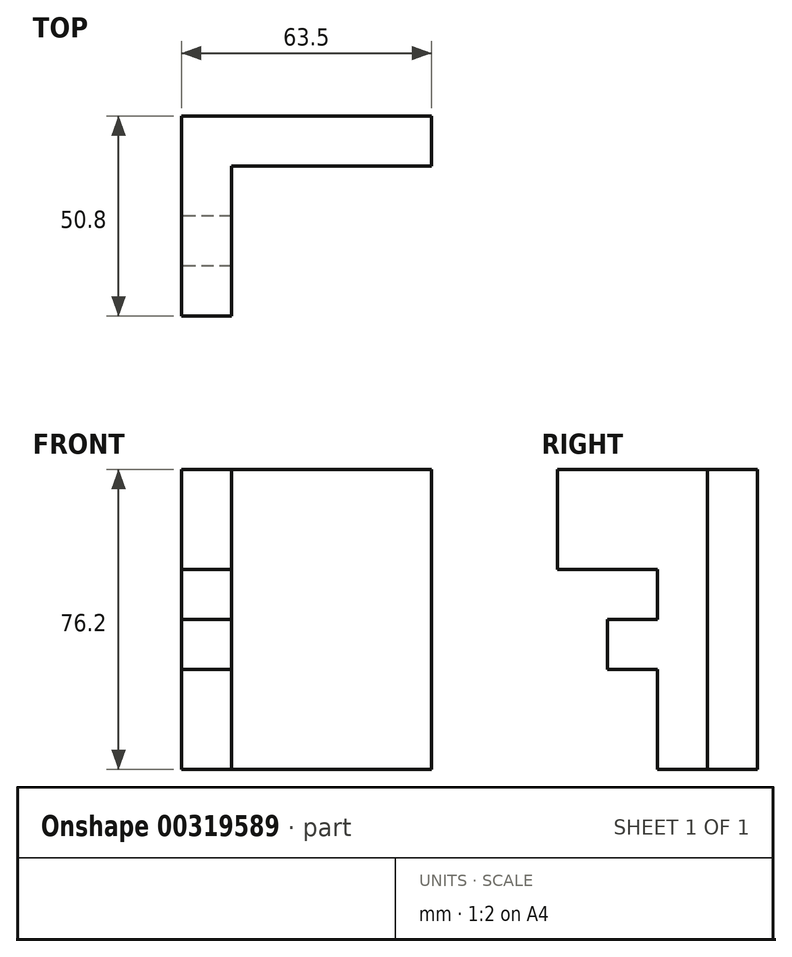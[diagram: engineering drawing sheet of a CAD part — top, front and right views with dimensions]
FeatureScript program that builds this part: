
annotation { "Feature Type Name" : "Feature", "Feature Type Description" : "" }
export const myFeature = defineFeature(function(context is Context, id is Id, definition is map)
    precondition{}
    {
        {
            var Q0;
            Q0=qCreatedBy(makeId("Right.planeOp"),FACE);
            var sketch = newSketch(context, id + "F0", { "sketchPlane" : qUnion([Q0])});
            skLineSegment(sketch, "E0", {"start": v(-44.52, -56.34) * mm, "end": v(-31.82, -56.34) * mm});
            skLineSegment(sketch, "E1", {"start": v(-44.52, -56.34) * mm, "end": v(-44.52, -30.94) * mm});
            skLineSegment(sketch, "E2", {"start": v(-44.52, -30.94) * mm, "end": v(-57.22, -30.94) * mm});
            skLineSegment(sketch, "E3", {"start": v(-57.22, -30.94) * mm, "end": v(-57.22, -18.24) * mm});
            skLineSegment(sketch, "E4", {"start": v(-57.22, -18.24) * mm, "end": v(-44.52, -18.24) * mm});
            skLineSegment(sketch, "E5", {"start": v(-44.52, -18.24) * mm, "end": v(-44.52, -5.54) * mm});
            skLineSegment(sketch, "E6", {"start": v(-44.52, -5.54) * mm, "end": v(-69.92, -5.54) * mm});
            skLineSegment(sketch, "E7", {"start": v(-69.92, -5.54) * mm, "end": v(-69.92, 19.86) * mm});
            skLineSegment(sketch, "E8", {"start": v(-69.92, 19.86) * mm, "end": v(-19.12, 19.86) * mm});
            skLineSegment(sketch, "E9", {"start": v(-19.12, 19.86) * mm, "end": v(-19.12, -56.34) * mm});
            skLineSegment(sketch, "E10", {"start": v(-19.12, -56.34) * mm, "end": v(-31.82, -56.34) * mm});
            skSolve(sketch);
        }
        {
            var Q0;
            Q0=makeQuery(id+"F0.imprint","IMPRINT",FACE,{"disambiguationData":[TD([[makeQuery(id+"F0.imprint","IMPRINT",EDGE,{"derivedFrom":sQuery(id+"F0.wireOp",EDGE,"E0")}),1.0]])]});
            extrude(context, id + "F1", {"entities" : qUnion([Q0]), "depth" : 12.7 * mm});
        }
        {
            var Q0;
            Q0=makeQuery(id+"F1.opExtrude","CAP_FACE",FACE,{"disambiguationData":[OSD([sQuery(id+"F0.wireOp",EDGE,"E0"),sQuery(id+"F0.wireOp",EDGE,"E1"),sQuery(id+"F0.wireOp",EDGE,"E2"),sQuery(id+"F0.wireOp",EDGE,"E3"),sQuery(id+"F0.wireOp",EDGE,"E4"),sQuery(id+"F0.wireOp",EDGE,"E5"),sQuery(id+"F0.wireOp",EDGE,"E6"),sQuery(id+"F0.wireOp",EDGE,"E7"),sQuery(id+"F0.wireOp",EDGE,"E8"),sQuery(id+"F0.wireOp",EDGE,"E9"),sQuery(id+"F0.wireOp",EDGE,"E10")])],"isStart":false});
            var sketch = newSketch(context, id + "F2", { "sketchPlane" : qUnion([Q0])});
            skLineSegment(sketch, "E11", {"start": v(-19.12, 19.86) * mm, "end": v(-31.82, 19.86) * mm});
            skLineSegment(sketch, "E12", {"start": v(-31.82, 19.86) * mm, "end": v(-31.82, -56.34) * mm});
            skLineSegment(sketch, "E13", {"start": v(-31.82, -56.34) * mm, "end": v(-19.12, -56.34) * mm});
            skLineSegment(sketch, "E14", {"start": v(-19.12, -56.34) * mm, "end": v(-19.12, 19.86) * mm});
            skSolve(sketch);
        }
        {
            var Q0;
            Q0=makeQuery(id+"F2.imprint","IMPRINT",FACE,{"disambiguationData":[TD([[makeQuery(id+"F2.imprint","IMPRINT",EDGE,{"derivedFrom":sQuery(id+"F2.wireOp",EDGE,"E11")}),-1.0]])]});
            extrude(context, id + "F3", {"entities" : qUnion([Q0]), "operationType" : NewBodyOperationType.ADD, "depth" : 50.8 * mm});
        }
    });
